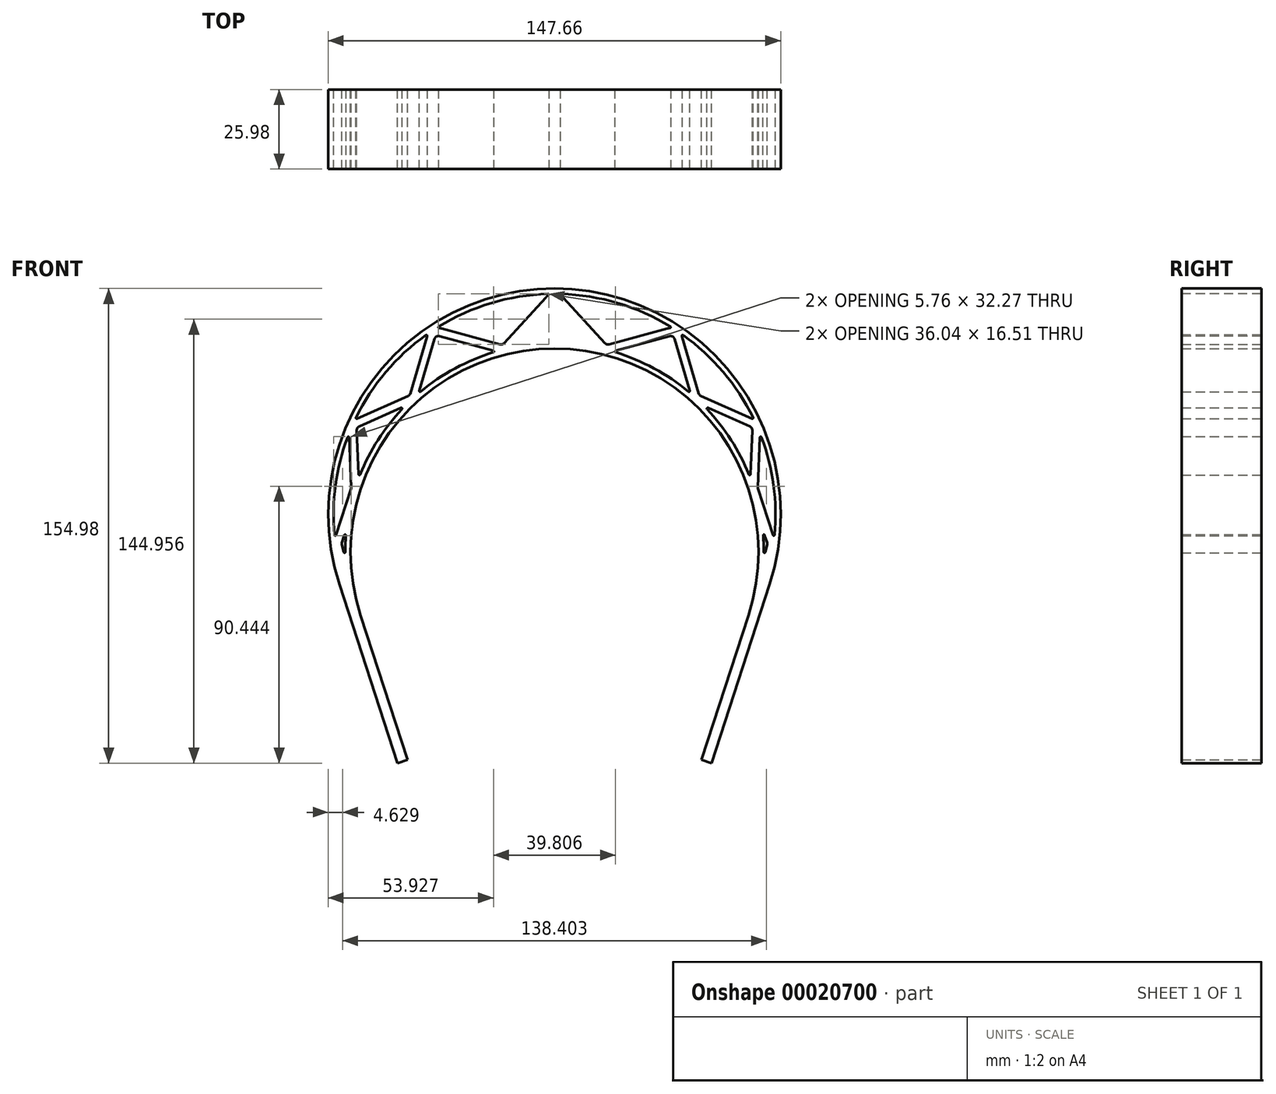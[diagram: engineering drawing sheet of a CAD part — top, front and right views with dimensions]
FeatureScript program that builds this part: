
annotation { "Feature Type Name" : "Feature", "Feature Type Description" : "" }
export const myFeature = defineFeature(function(context is Context, id is Id, definition is map)
    precondition{}
    {
        {
            var Q0;
            Q0=qCreatedBy(makeId("Front.planeOp"),FACE);
            var sketch = newSketch(context, id + "F0", { "sketchPlane" : qUnion([Q0])});
            skCircle(sketch, "E0.cCircle", {"center": v(0, 0) * mm, "radius": 78.86 * mm});
            skLineSegment(sketch, "E0.0", {"start": v(57.3, -78.86) * mm, "end": v(-57.3, -78.86) * mm, "construction": true});
            skLineSegment(sketch, "E0.1", {"start": v(-57.3, -78.86) * mm, "end": v(-92.7, 30.12) * mm, "construction": true});
            skLineSegment(sketch, "E0.2", {"start": v(-92.7, 30.12) * mm, "end": v(0, 97.48) * mm, "construction": true});
            skLineSegment(sketch, "E0.3", {"start": v(0, 97.48) * mm, "end": v(92.7, 30.12) * mm, "construction": true});
            skLineSegment(sketch, "E0.4", {"start": v(92.7, 30.12) * mm, "end": v(57.3, -78.86) * mm, "construction": true});
            skPoint(sketch, "E0.0.midPoint", {"position": v(0, -78.86) * mm});
            skLineSegment(sketch, "E1", {"start": v(-75, -24.37) * mm, "end": v(75, -24.37) * mm, "construction": true});
            skArc(sketch, "E2", {"start": v(79.18, -11.5) * mm, "mid": v(0, 97.48) * mm, "end": v(-79.18, -11.5) * mm});
            skSolve(sketch);
        }
        {
            var Q0;
            Q0=qCreatedBy(makeId("Front.planeOp"),FACE);
            var sketch = newSketch(context, id + "F1", { "sketchPlane" : qUnion([Q0])});
            skArc(sketch, "E3.0", {"start": v(0, 76.86) * mm, "mid": v(-62.18, 45.18) * mm, "end": v(-73.1, -23.75) * mm});
            skArc(sketch, "E4.0", {"start": v(0, 99.48) * mm, "mid": v(-68.97, 64.33) * mm, "end": v(-81.08, -12.12) * mm});
            skLineSegment(sketch, "E5", {"start": v(-81.08, -12.12) * mm, "end": v(-59.2, -79.48) * mm});
            skLineSegment(sketch, "E6", {"start": v(-73.1, -23.75) * mm, "end": v(-55.4, -78.24) * mm});
            skLineSegment(sketch, "E7", {"start": v(-55.4, -78.24) * mm, "end": v(-59.2, -79.48) * mm});
            skLineSegment(sketch, "E8", {"start": v(0, 76.86) * mm, "end": v(0, 99.48) * mm});
            skSolve(sketch);
        }
        {
            var Q0;
            Q0=qCreatedBy(makeId("Front.planeOp"),FACE);
            var sketch = newSketch(context, id + "F2", { "sketchPlane" : qUnion([Q0])});
            skArc(sketch, "E9.0", {"start": v(-76.8, -17.94) * mm, "mid": v(-61.78, 49.01) * mm, "end": v(0, 78.86) * mm});
            skArc(sketch, "E9.1", {"start": v(0, 97.48) * mm, "mid": v(-69.31, 60.34) * mm, "end": v(-76.8, -17.94) * mm});
            skLineSegment(sketch, "E10", {"start": v(0, 78.86) * mm, "end": v(0, 97.48) * mm});
            skLineSegment(sketch, "E11", {"start": v(0, 14.22) * mm, "end": v(0, 0) * mm, "construction": true});
            skLineSegment(sketch, "E12", {"start": v(0, 7.11) * mm, "end": v(-116.66, -30.94) * mm, "construction": true});
            skLineSegment(sketch, "E13.1.0", {"start": v(0, 7.11) * mm, "end": v(-122.58, 1.49) * mm, "construction": true});
            skLineSegment(sketch, "E13.2.0", {"start": v(0, 7.11) * mm, "end": v(-119.65, 34.32) * mm, "construction": true});
            skLineSegment(sketch, "E13.3.0", {"start": v(0, 7.11) * mm, "end": v(-108.1, 65.19) * mm, "construction": true});
            skLineSegment(sketch, "E13.4.0", {"start": v(0, 7.11) * mm, "end": v(-88.73, 91.86) * mm, "construction": true});
            skLineSegment(sketch, "E13.5.0", {"start": v(0, 7.11) * mm, "end": v(-62.97, 112.43) * mm, "construction": true});
            skLineSegment(sketch, "E13.6.0", {"start": v(0, 7.11) * mm, "end": v(-32.66, 125.39) * mm, "construction": true});
            skPoint(sketch, "E13.center", {"position": v(0, 7.11) * mm});
            skLineSegment(sketch, "E13.anchor2", {"start": v(0, 7.11) * mm, "end": v(0, 129.81) * mm, "construction": true});
            skLineSegment(sketch, "E14", {"start": v(-76.8, -17.94) * mm, "end": v(-81.58, 2.55) * mm, "construction": true});
            skLineSegment(sketch, "E15", {"start": v(-81.51, 4.15) * mm, "end": v(-75.23, 23.67) * mm, "construction": true});
            skLineSegment(sketch, "E16", {"start": v(-75.08, 24.72) * mm, "end": v(-76, 45.95) * mm, "construction": true});
            skLineSegment(sketch, "E17", {"start": v(-74.23, 48.82) * mm, "end": v(-54.62, 57.5) * mm, "construction": true});
            skLineSegment(sketch, "E18", {"start": v(-52.96, 59.4) * mm, "end": v(-46.64, 80.92) * mm, "construction": true});
            skLineSegment(sketch, "E19", {"start": v(-42.98, 82.97) * mm, "end": v(-20.93, 76.98) * mm, "construction": true});
            skLineSegment(sketch, "E20", {"start": v(-17.93, 77.85) * mm, "end": v(-2.22, 95.05) * mm, "construction": true});
            skLineSegment(sketch, "E21", {"start": v(2.22, 95.05) * mm, "end": v(9.94, 86.6) * mm, "construction": true});
            skPoint(sketch, "E22.visualSharp", {"position": v(0, 97.48) * mm});
            skArc(sketch, "E22.filletArc", {"start": v(2.22, 95.05) * mm, "mid": v(0, 96.03) * mm, "end": v(-2.22, 95.05) * mm, "construction": true});
            skPoint(sketch, "E23.visualSharp", {"position": v(-19.16, 76.5) * mm});
            skArc(sketch, "E23.filletArc", {"start": v(-20.93, 76.98) * mm, "mid": v(-19.3, 77) * mm, "end": v(-17.93, 77.85) * mm, "construction": true});
            skPoint(sketch, "E24.visualSharp", {"position": v(-45.82, 83.74) * mm});
            skArc(sketch, "E24.filletArc", {"start": v(-42.98, 82.97) * mm, "mid": v(-45.23, 82.69) * mm, "end": v(-46.64, 80.92) * mm, "construction": true});
            skPoint(sketch, "E25.visualSharp", {"position": v(-53.35, 58.07) * mm});
            skArc(sketch, "E25.filletArc", {"start": v(-54.62, 57.5) * mm, "mid": v(-53.58, 58.27) * mm, "end": v(-52.96, 59.4) * mm, "construction": true});
            skPoint(sketch, "E26.visualSharp", {"position": v(-76.1, 48) * mm});
            skArc(sketch, "E26.filletArc", {"start": v(-74.23, 48.82) * mm, "mid": v(-75.56, 47.66) * mm, "end": v(-76, 45.95) * mm, "construction": true});
            skPoint(sketch, "E27.visualSharp", {"position": v(-75.06, 24.18) * mm});
            skArc(sketch, "E27.filletArc", {"start": v(-75.23, 23.67) * mm, "mid": v(-75.1, 24.19) * mm, "end": v(-75.08, 24.72) * mm, "construction": true});
            skPoint(sketch, "E28.visualSharp", {"position": v(-81.77, 3.36) * mm});
            skArc(sketch, "E28.filletArc", {"start": v(-81.51, 4.15) * mm, "mid": v(-81.65, 3.35) * mm, "end": v(-81.58, 2.55) * mm, "construction": true});
            skLineSegment(sketch, "E29.0", {"start": v(-78.25, -18.28) * mm, "end": v(-83.04, 2.2) * mm});
            skArc(sketch, "E29.1", {"start": v(-82.94, 4.61) * mm, "mid": v(-83.15, 3.42) * mm, "end": v(-83.04, 2.2) * mm});
            skLineSegment(sketch, "E29.2", {"start": v(-82.94, 4.61) * mm, "end": v(-76.65, 24.13) * mm});
            skArc(sketch, "E29.3", {"start": v(-76.65, 24.13) * mm, "mid": v(-76.6, 24.39) * mm, "end": v(-76.58, 24.65) * mm});
            skLineSegment(sketch, "E29.4", {"start": v(-76.58, 24.65) * mm, "end": v(-77.5, 45.89) * mm});
            skArc(sketch, "E29.5", {"start": v(-74.83, 50.2) * mm, "mid": v(-76.83, 48.45) * mm, "end": v(-77.5, 45.89) * mm});
            skLineSegment(sketch, "E29.6", {"start": v(-74.83, 50.2) * mm, "end": v(-55.23, 58.88) * mm});
            skArc(sketch, "E29.7", {"start": v(-55.23, 58.88) * mm, "mid": v(-54.71, 59.26) * mm, "end": v(-54.4, 59.83) * mm});
            skLineSegment(sketch, "E29.8", {"start": v(-54.4, 59.83) * mm, "end": v(-48.08, 81.34) * mm});
            skArc(sketch, "E29.9", {"start": v(-42.59, 84.41) * mm, "mid": v(-45.96, 84) * mm, "end": v(-48.08, 81.34) * mm});
            skLineSegment(sketch, "E29.10", {"start": v(-42.59, 84.41) * mm, "end": v(-20.53, 78.42) * mm});
            skArc(sketch, "E29.11", {"start": v(-20.53, 78.42) * mm, "mid": v(-19.72, 78.43) * mm, "end": v(-19.03, 78.86) * mm});
            skLineSegment(sketch, "E29.12", {"start": v(-19.03, 78.86) * mm, "end": v(-3.32, 96.06) * mm});
            skArc(sketch, "E29.13", {"start": v(3.32, 96.06) * mm, "mid": v(0, 97.53) * mm, "end": v(-3.32, 96.06) * mm});
            skLineSegment(sketch, "E30.0", {"start": v(-75.33, -17.6) * mm, "end": v(-80.12, 2.89) * mm});
            skArc(sketch, "E30.1", {"start": v(-80.08, 3.7) * mm, "mid": v(-80.16, 3.3) * mm, "end": v(-80.12, 2.89) * mm});
            skLineSegment(sketch, "E30.2", {"start": v(-80.08, 3.7) * mm, "end": v(-73.8, 23.2) * mm});
            skArc(sketch, "E30.3", {"start": v(-73.8, 23.2) * mm, "mid": v(-73.62, 23.98) * mm, "end": v(-73.59, 24.78) * mm});
            skLineSegment(sketch, "E30.4", {"start": v(-73.59, 24.78) * mm, "end": v(-74.5, 46.02) * mm});
            skArc(sketch, "E30.5", {"start": v(-73.62, 47.45) * mm, "mid": v(-74.28, 46.87) * mm, "end": v(-74.5, 46.02) * mm});
            skLineSegment(sketch, "E30.6", {"start": v(-73.62, 47.45) * mm, "end": v(-54.02, 56.14) * mm});
            skArc(sketch, "E30.7", {"start": v(-54.02, 56.14) * mm, "mid": v(-52.46, 57.28) * mm, "end": v(-51.52, 58.98) * mm});
            skLineSegment(sketch, "E30.8", {"start": v(-51.52, 58.98) * mm, "end": v(-45.2, 80.5) * mm});
            skArc(sketch, "E30.9", {"start": v(-43.37, 81.52) * mm, "mid": v(-44.5, 81.38) * mm, "end": v(-45.2, 80.5) * mm});
            skLineSegment(sketch, "E30.10", {"start": v(-43.37, 81.52) * mm, "end": v(-21.32, 75.53) * mm});
            skArc(sketch, "E30.11", {"start": v(-21.32, 75.53) * mm, "mid": v(-18.89, 75.55) * mm, "end": v(-16.82, 76.84) * mm});
            skLineSegment(sketch, "E30.12", {"start": v(-16.82, 76.84) * mm, "end": v(-1.1, 94.04) * mm});
            skArc(sketch, "E30.13", {"start": v(1.1, 94.04) * mm, "mid": v(0, 94.53) * mm, "end": v(-1.1, 94.04) * mm});
            skSolve(sketch);
        }
        {
            var Q0;
            Q0 = qSketchRegion(id + "F1", true);
            extrude(context, id + "F3", {"entities" : qUnion([Q0]), "depth" : 15 * mm});
        }
        {
            var Q0;
            {var subQ1=sQuery(id+"F2.wireOp",EDGE,"E9.0");var subQ5=sQuery(id+"F2.wireOp",EDGE,"E10");var subQ7=makeQuery(id+"F2.imprint","INTERSECT",VERTEX,{"derivedFrom":[subQ1,subQ5]});Q0=makeQuery(id+"F2.imprint","IMPRINT",FACE,{"disambiguationData":[TD([[makeQuery(id+"F2.imprint","IMPRINT",EDGE,{"disambiguationData":[TD([[subQ7,1.0]])],"derivedFrom":subQ1}),1.0]])]});}
            var Q1;
            {var subQ4=sQuery(id+"F2.wireOp",EDGE,"E29.10");Q1=makeQuery(id+"F2.imprint","IMPRINT",FACE,{"disambiguationData":[TD([[makeQuery(id+"F2.imprint","IMPRINT",EDGE,{"derivedFrom":subQ4}),1.0]])]});}
            var Q2;
            {var subQ3=sQuery(id+"F2.wireOp",EDGE,"E30.9");Q2=makeQuery(id+"F2.imprint","IMPRINT",FACE,{"disambiguationData":[TD([[makeQuery(id+"F2.imprint","IMPRINT",EDGE,{"derivedFrom":subQ3}),1.0]])]});}
            var Q3;
            {var subQ4=sQuery(id+"F2.wireOp",EDGE,"E29.6");Q3=makeQuery(id+"F2.imprint","IMPRINT",FACE,{"disambiguationData":[TD([[makeQuery(id+"F2.imprint","IMPRINT",EDGE,{"derivedFrom":subQ4}),1.0]])]});}
            var Q4;
            {var subQ3=sQuery(id+"F2.wireOp",EDGE,"E30.5");Q4=makeQuery(id+"F2.imprint","IMPRINT",FACE,{"disambiguationData":[TD([[makeQuery(id+"F2.imprint","IMPRINT",EDGE,{"derivedFrom":subQ3}),1.0]])]});}
            var Q5;
            {var subQ3=sQuery(id+"F2.wireOp",EDGE,"E29.3");Q5=makeQuery(id+"F2.imprint","IMPRINT",FACE,{"disambiguationData":[TD([[makeQuery(id+"F2.imprint","IMPRINT",EDGE,{"derivedFrom":subQ3}),1.0]])]});}
            var Q6;
            {var subQ3=sQuery(id+"F2.wireOp",EDGE,"E30.1");Q6=makeQuery(id+"F2.imprint","IMPRINT",FACE,{"disambiguationData":[TD([[makeQuery(id+"F2.imprint","IMPRINT",EDGE,{"derivedFrom":subQ3}),1.0]])]});}
            var Q7;
            Q7=makeQuery(id+"F3.opExtrude","CAP_FACE",FACE,{"disambiguationData":[OSD([sQuery(id+"F1.wireOp",EDGE,"E3.0"),sQuery(id+"F1.wireOp",EDGE,"E4.0"),sQuery(id+"F1.wireOp",EDGE,"E5"),sQuery(id+"F1.wireOp",EDGE,"E6"),sQuery(id+"F1.wireOp",EDGE,"E7"),sQuery(id+"F1.wireOp",EDGE,"E8")])],"isStart":false});
            extrude(context, id + "F4", {"entities" : qUnion([Q0, Q1, Q2, Q3, Q4, Q5, Q6]), "endBound" : BoundingType.UP_TO_SURFACE, "endBoundEntityFace" : qUnion([Q7]), "depth" : 25 * mm});
        }
        {
            var Q0;
            Q0=makeQuery(id+"F4.opExtrude","SWEPT_EDGE",EDGE,{"disambiguationData":[OSD([sQuery(id+"F2.wireOp",EDGE,"E9.0"),sQuery(id+"F2.wireOp",EDGE,"E30.12")])]});
            var Q1;
            Q1=makeQuery(id+"F4.opExtrude","SWEPT_EDGE",EDGE,{"disambiguationData":[OSD([sQuery(id+"F2.wireOp",EDGE,"E9.0"),sQuery(id+"F2.wireOp",EDGE,"E30.10")])]});
            var Q2;
            Q2=makeQuery(id+"F4.opExtrude","SWEPT_EDGE",EDGE,{"disambiguationData":[OSD([sQuery(id+"F2.wireOp",EDGE,"E9.1"),sQuery(id+"F2.wireOp",EDGE,"E29.13")])]});
            var Q3;
            {var subQ0=sQuery(id+"F2.wireOp",EDGE,"E9.1");var subQ1=sQuery(id+"F2.wireOp",EDGE,"E29.9");Q3=makeQuery(id+"F4.opExtrude","SWEPT_EDGE",EDGE,{"disambiguationData":[OSD([subQ0,subQ1]),TDD([makeQuery(id+"F2.imprint","INTERSECT",VERTEX,{"disambiguationData":[OD(0.0)],"derivedFrom":[subQ0,subQ1]})])]});}
            var Q4;
            Q4=makeQuery(id+"F4.opExtrude","SWEPT_EDGE",EDGE,{"disambiguationData":[OSD([sQuery(id+"F2.wireOp",EDGE,"E9.0"),sQuery(id+"F2.wireOp",EDGE,"E30.8")])]});
            var Q5;
            Q5=makeQuery(id+"F4.opExtrude","SWEPT_EDGE",EDGE,{"disambiguationData":[OSD([sQuery(id+"F2.wireOp",EDGE,"E9.1"),sQuery(id+"F2.wireOp",EDGE,"E29.5")])]});
            var Q6;
            {var subQ0=sQuery(id+"F2.wireOp",EDGE,"E9.1");var subQ1=sQuery(id+"F2.wireOp",EDGE,"E29.9");Q6=makeQuery(id+"F4.opExtrude","SWEPT_EDGE",EDGE,{"disambiguationData":[OSD([subQ0,subQ1]),TDD([makeQuery(id+"F2.imprint","INTERSECT",VERTEX,{"disambiguationData":[OD(1.0)],"derivedFrom":[subQ0,subQ1]})])]});}
            var Q7;
            Q7=makeQuery(id+"F4.opExtrude","SWEPT_EDGE",EDGE,{"disambiguationData":[OSD([sQuery(id+"F2.wireOp",EDGE,"E9.0"),sQuery(id+"F2.wireOp",EDGE,"E30.6")])]});
            var Q8;
            Q8=makeQuery(id+"F4.opExtrude","SWEPT_EDGE",EDGE,{"disambiguationData":[OSD([sQuery(id+"F2.wireOp",EDGE,"E9.0"),sQuery(id+"F2.wireOp",EDGE,"E30.4")])]});
            var Q9;
            Q9=makeQuery(id+"F4.opExtrude","SWEPT_EDGE",EDGE,{"disambiguationData":[OSD([sQuery(id+"F2.wireOp",EDGE,"E9.1"),sQuery(id+"F2.wireOp",EDGE,"E29.2")])]});
            var Q10;
            Q10=makeQuery(id+"F4.opExtrude","SWEPT_EDGE",EDGE,{"disambiguationData":[OSD([sQuery(id+"F2.wireOp",EDGE,"E9.1"),sQuery(id+"F2.wireOp",EDGE,"E29.4")])]});
            var Q11;
            Q11=makeQuery(id+"F4.opExtrude","SWEPT_EDGE",EDGE,{"disambiguationData":[OSD([sQuery(id+"F2.wireOp",EDGE,"E9.0"),sQuery(id+"F2.wireOp",EDGE,"E30.2")])]});
            var Q12;
            Q12=makeQuery(id+"F4.opExtrude","SWEPT_EDGE",EDGE,{"disambiguationData":[OSD([sQuery(id+"F2.wireOp",EDGE,"E9.0"),sQuery(id+"F2.wireOp",EDGE,"E30.0")])]});
            fillet(context, id + "F5", {"entities" : qUnion([Q0, Q1, Q2, Q3, Q4, Q5, Q6, Q7, Q8, Q9, Q10, Q11, Q12]), "radius" : 0.3 * mm, "tangentPropagation" : true, "allowEdgeOverflow" : false});
        }
        {
            var Q0;
            Q0=makeQuery(id+"F4.opExtrude","SWEPT_BODY",BODY,{"disambiguationData":[OSD([sQuery(id+"F2.wireOp",EDGE,"E9.0"),sQuery(id+"F2.wireOp",EDGE,"E30.0"),sQuery(id+"F2.wireOp",EDGE,"E30.1"),sQuery(id+"F2.wireOp",EDGE,"E30.2")])]});
            var Q1;
            Q1=makeQuery(id+"F4.opExtrude","SWEPT_BODY",BODY,{"disambiguationData":[OSD([sQuery(id+"F2.wireOp",EDGE,"E9.0"),sQuery(id+"F2.wireOp",EDGE,"E30.4"),sQuery(id+"F2.wireOp",EDGE,"E30.5"),sQuery(id+"F2.wireOp",EDGE,"E30.6")])]});
            var Q2;
            Q2=makeQuery(id+"F4.opExtrude","SWEPT_BODY",BODY,{"disambiguationData":[OSD([sQuery(id+"F2.wireOp",EDGE,"E9.0"),sQuery(id+"F2.wireOp",EDGE,"E30.8"),sQuery(id+"F2.wireOp",EDGE,"E30.9"),sQuery(id+"F2.wireOp",EDGE,"E30.10")])]});
            var Q3;
            Q3=makeQuery(id+"F4.opExtrude","SWEPT_BODY",BODY,{"disambiguationData":[OSD([sQuery(id+"F2.wireOp",EDGE,"E9.0"),sQuery(id+"F2.wireOp",EDGE,"E10"),sQuery(id+"F2.wireOp",EDGE,"E30.12"),sQuery(id+"F2.wireOp",EDGE,"E30.13")])]});
            var Q4;
            Q4=makeQuery(id+"F4.opExtrude","SWEPT_BODY",BODY,{"disambiguationData":[OSD([sQuery(id+"F2.wireOp",EDGE,"E9.1"),sQuery(id+"F2.wireOp",EDGE,"E29.9"),sQuery(id+"F2.wireOp",EDGE,"E29.10"),sQuery(id+"F2.wireOp",EDGE,"E29.11"),sQuery(id+"F2.wireOp",EDGE,"E29.12"),sQuery(id+"F2.wireOp",EDGE,"E29.13")])]});
            var Q5;
            Q5=makeQuery(id+"F4.opExtrude","SWEPT_BODY",BODY,{"disambiguationData":[OSD([sQuery(id+"F2.wireOp",EDGE,"E9.1"),sQuery(id+"F2.wireOp",EDGE,"E29.5"),sQuery(id+"F2.wireOp",EDGE,"E29.6"),sQuery(id+"F2.wireOp",EDGE,"E29.7"),sQuery(id+"F2.wireOp",EDGE,"E29.8"),sQuery(id+"F2.wireOp",EDGE,"E29.9")])]});
            var Q6;
            Q6=makeQuery(id+"F4.opExtrude","SWEPT_BODY",BODY,{"disambiguationData":[OSD([sQuery(id+"F2.wireOp",EDGE,"E9.1"),sQuery(id+"F2.wireOp",EDGE,"E29.2"),sQuery(id+"F2.wireOp",EDGE,"E29.3"),sQuery(id+"F2.wireOp",EDGE,"E29.4")])]});
            var Q7;
            Q7=makeQuery(id+"F3.opExtrude","SWEPT_BODY",BODY,{"disambiguationData":[OSD([sQuery(id+"F1.wireOp",EDGE,"E3.0"),sQuery(id+"F1.wireOp",EDGE,"E4.0"),sQuery(id+"F1.wireOp",EDGE,"E5"),sQuery(id+"F1.wireOp",EDGE,"E6"),sQuery(id+"F1.wireOp",EDGE,"E7"),sQuery(id+"F1.wireOp",EDGE,"E8")])]});
            booleanBodies(context, id + "F6", {"operationType" : BooleanOperationType.SUBTRACTION, "tools" : qUnion([Q0, Q1, Q2, Q3, Q4, Q5, Q6]), "targets" : qUnion([Q7])});
        }
        {
            var Q0;
            Q0=makeQuery(id+"F3.opExtrude","SWEPT_BODY",BODY,{"disambiguationData":[OSD([sQuery(id+"F1.wireOp",EDGE,"E3.0"),sQuery(id+"F1.wireOp",EDGE,"E4.0"),sQuery(id+"F1.wireOp",EDGE,"E5"),sQuery(id+"F1.wireOp",EDGE,"E6"),sQuery(id+"F1.wireOp",EDGE,"E7"),sQuery(id+"F1.wireOp",EDGE,"E8")])]});
            var Q1;
            Q1=qCreatedBy(makeId("Front.planeOp"),FACE);
            mirror(context, id + "F7", {"operationType" : NewBodyOperationType.ADD, "entities" : qUnion([Q0]), "mirrorPlane" : qUnion([Q1])});
        }
        {
            var Q0;
            Q0=makeQuery(id+"F3.opExtrude","SWEPT_BODY",BODY,{"disambiguationData":[OSD([sQuery(id+"F1.wireOp",EDGE,"E3.0"),sQuery(id+"F1.wireOp",EDGE,"E4.0"),sQuery(id+"F1.wireOp",EDGE,"E5"),sQuery(id+"F1.wireOp",EDGE,"E6"),sQuery(id+"F1.wireOp",EDGE,"E7"),sQuery(id+"F1.wireOp",EDGE,"E8")])]});
            var Q1;
            Q1=qCreatedBy(makeId("Right.planeOp"),FACE);
            mirror(context, id + "F8", {"operationType" : NewBodyOperationType.ADD, "entities" : qUnion([Q0]), "mirrorPlane" : qUnion([Q1])});
        }
        {
            var Q0;
            Q0=makeQuery(id+"F3.opExtrude","SWEPT_BODY",BODY,{"disambiguationData":[OSD([sQuery(id+"F1.wireOp",EDGE,"E3.0"),sQuery(id+"F1.wireOp",EDGE,"E4.0"),sQuery(id+"F1.wireOp",EDGE,"E5"),sQuery(id+"F1.wireOp",EDGE,"E6"),sQuery(id+"F1.wireOp",EDGE,"E7"),sQuery(id+"F1.wireOp",EDGE,"E8")])]});
            var Q1;
            Q1=sQuery(id+"F2.wireOp",VERTEX,"E11.end");
            transform(context, id + "F9", {"entities" : qUnion([Q0]), "transformType" : TransformType.SCALE_UNIFORMLY, "scale" : 0.87, "makeCopy" : false, "scalePoint" : qUnion([Q1])});
        }
    });
